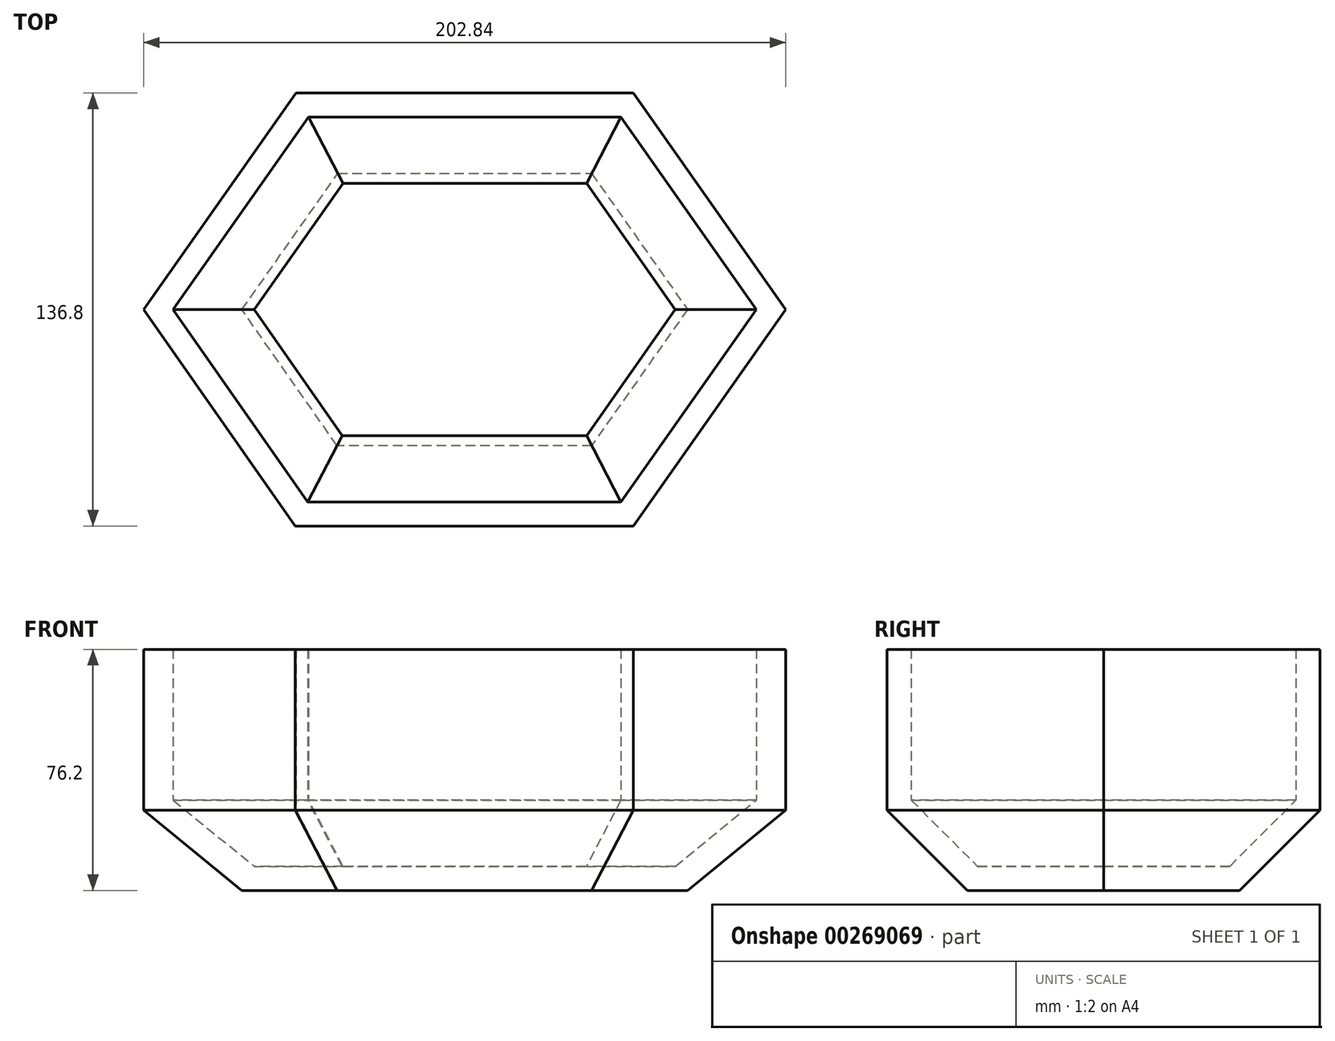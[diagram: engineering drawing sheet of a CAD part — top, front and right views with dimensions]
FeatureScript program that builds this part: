
annotation { "Feature Type Name" : "Feature", "Feature Type Description" : "" }
export const myFeature = defineFeature(function(context is Context, id is Id, definition is map)
    precondition{}
    {
        {
            var Q0;
            Q0=qCreatedBy(makeId("Top.planeOp"),FACE);
            var sketch = newSketch(context, id + "F0", { "sketchPlane" : qUnion([Q0])});
            skLineSegment(sketch, "E0", {"start": v(0, 43) * mm, "end": v(-52.83, 43) * mm});
            skLineSegment(sketch, "E1", {"start": v(-52.83, 43) * mm, "end": v(-75.56, 0) * mm});
            skLineSegment(sketch, "E2", {"start": v(-52.83, 43) * mm, "end": v(-52.83, 68.4) * mm});
            skLineSegment(sketch, "E3", {"start": v(0, 43) * mm, "end": v(53.75, 43) * mm});
            skLineSegment(sketch, "E4", {"start": v(53.75, 43) * mm, "end": v(76.48, 0) * mm});
            skLineSegment(sketch, "E5", {"start": v(76.48, 0) * mm, "end": v(53.75, -43) * mm});
            skLineSegment(sketch, "E6", {"start": v(53.75, -43) * mm, "end": v(-52.83, -43) * mm});
            skLineSegment(sketch, "E7", {"start": v(-75.56, 0) * mm, "end": v(-52.83, -43) * mm});
            skLineSegment(sketch, "E8", {"start": v(-52.83, 68.4) * mm, "end": v(53.75, 68.4) * mm});
            skLineSegment(sketch, "E9", {"start": v(53.75, 68.4) * mm, "end": v(53.75, 43) * mm});
            skLineSegment(sketch, "E10", {"start": v(53.75, -43) * mm, "end": v(53.75, -68.4) * mm});
            skLineSegment(sketch, "E11", {"start": v(53.75, -68.4) * mm, "end": v(-53.14, -68.4) * mm});
            skLineSegment(sketch, "E12", {"start": v(-53.14, -68.4) * mm, "end": v(-52.83, -43) * mm});
            skLineSegment(sketch, "E13", {"start": v(53.75, -68.4) * mm, "end": v(101.88, 0) * mm});
            skLineSegment(sketch, "E14", {"start": v(101.88, 0) * mm, "end": v(53.75, 68.4) * mm});
            skLineSegment(sketch, "E15", {"start": v(76.48, 0) * mm, "end": v(101.88, 0) * mm});
            skLineSegment(sketch, "E16", {"start": v(-75.56, 0) * mm, "end": v(-100.96, 0) * mm});
            skLineSegment(sketch, "E17", {"start": v(-100.96, 0) * mm, "end": v(-53.14, -68.4) * mm});
            skLineSegment(sketch, "E18", {"start": v(-52.83, 68.4) * mm, "end": v(-100.96, 0) * mm});
            skSolve(sketch);
        }
        {
            var Q0;
            Q0=makeQuery(id+"F0.imprint","IMPRINT",FACE,{"disambiguationData":[TD([[makeQuery(id+"F0.imprint","IMPRINT",EDGE,{"derivedFrom":sQuery(id+"F0.wireOp",EDGE,"E0")}),-1.0]])]});
            var Q1;
            Q1=makeQuery(id+"F0.imprint","IMPRINT",FACE,{"disambiguationData":[TD([[makeQuery(id+"F0.imprint","IMPRINT",EDGE,{"derivedFrom":sQuery(id+"F0.wireOp",EDGE,"E1")}),-1.0]])]});
            var Q2;
            Q2=makeQuery(id+"F0.imprint","IMPRINT",FACE,{"disambiguationData":[TD([[makeQuery(id+"F0.imprint","IMPRINT",EDGE,{"derivedFrom":sQuery(id+"F0.wireOp",EDGE,"E4")}),1.0]])]});
            var Q3;
            Q3=makeQuery(id+"F0.imprint","IMPRINT",FACE,{"disambiguationData":[TD([[makeQuery(id+"F0.imprint","IMPRINT",EDGE,{"derivedFrom":sQuery(id+"F0.wireOp",EDGE,"E0")}),1.0]])]});
            var Q4;
            Q4=makeQuery(id+"F0.imprint","IMPRINT",FACE,{"disambiguationData":[TD([[makeQuery(id+"F0.imprint","IMPRINT",EDGE,{"derivedFrom":sQuery(id+"F0.wireOp",EDGE,"E5")}),1.0]])]});
            var Q5;
            Q5=makeQuery(id+"F0.imprint","IMPRINT",FACE,{"disambiguationData":[TD([[makeQuery(id+"F0.imprint","IMPRINT",EDGE,{"derivedFrom":sQuery(id+"F0.wireOp",EDGE,"E6")}),1.0]])]});
            var Q6;
            Q6=makeQuery(id+"F0.imprint","IMPRINT",FACE,{"disambiguationData":[TD([[makeQuery(id+"F0.imprint","IMPRINT",EDGE,{"derivedFrom":sQuery(id+"F0.wireOp",EDGE,"E7")}),-1.0]])]});
            extrude(context, id + "F1", {"entities" : qUnion([Q0, Q1, Q2, Q3, Q4, Q5, Q6]), "depth" : 76.2 * mm});
        }
        {
            var Q0;
            Q0=makeQuery(id+"F1.opExtrude","CAP_FACE",FACE,{"disambiguationData":[OSD([sQuery(id+"F0.wireOp",EDGE,"E8"),sQuery(id+"F0.wireOp",EDGE,"E11"),sQuery(id+"F0.wireOp",EDGE,"E13"),sQuery(id+"F0.wireOp",EDGE,"E14"),sQuery(id+"F0.wireOp",EDGE,"E17"),sQuery(id+"F0.wireOp",EDGE,"E18")])],"isStart":true});
            chamfer(context, id + "F2", {"entities" : qUnion([Q0]), "width" : 25.4 * mm, "tangentPropagation" : true});
        }
        {
            var Q0;
            Q0=makeQuery(id+"F1.opExtrude","CAP_FACE",FACE,{"disambiguationData":[OSD([sQuery(id+"F0.wireOp",EDGE,"E8"),sQuery(id+"F0.wireOp",EDGE,"E11"),sQuery(id+"F0.wireOp",EDGE,"E13"),sQuery(id+"F0.wireOp",EDGE,"E14"),sQuery(id+"F0.wireOp",EDGE,"E17"),sQuery(id+"F0.wireOp",EDGE,"E18")])],"isStart":false});
            shell(context, id + "F3", {"entities" : qUnion([Q0]), "thickness" : 7.62 * mm});
        }
    });
